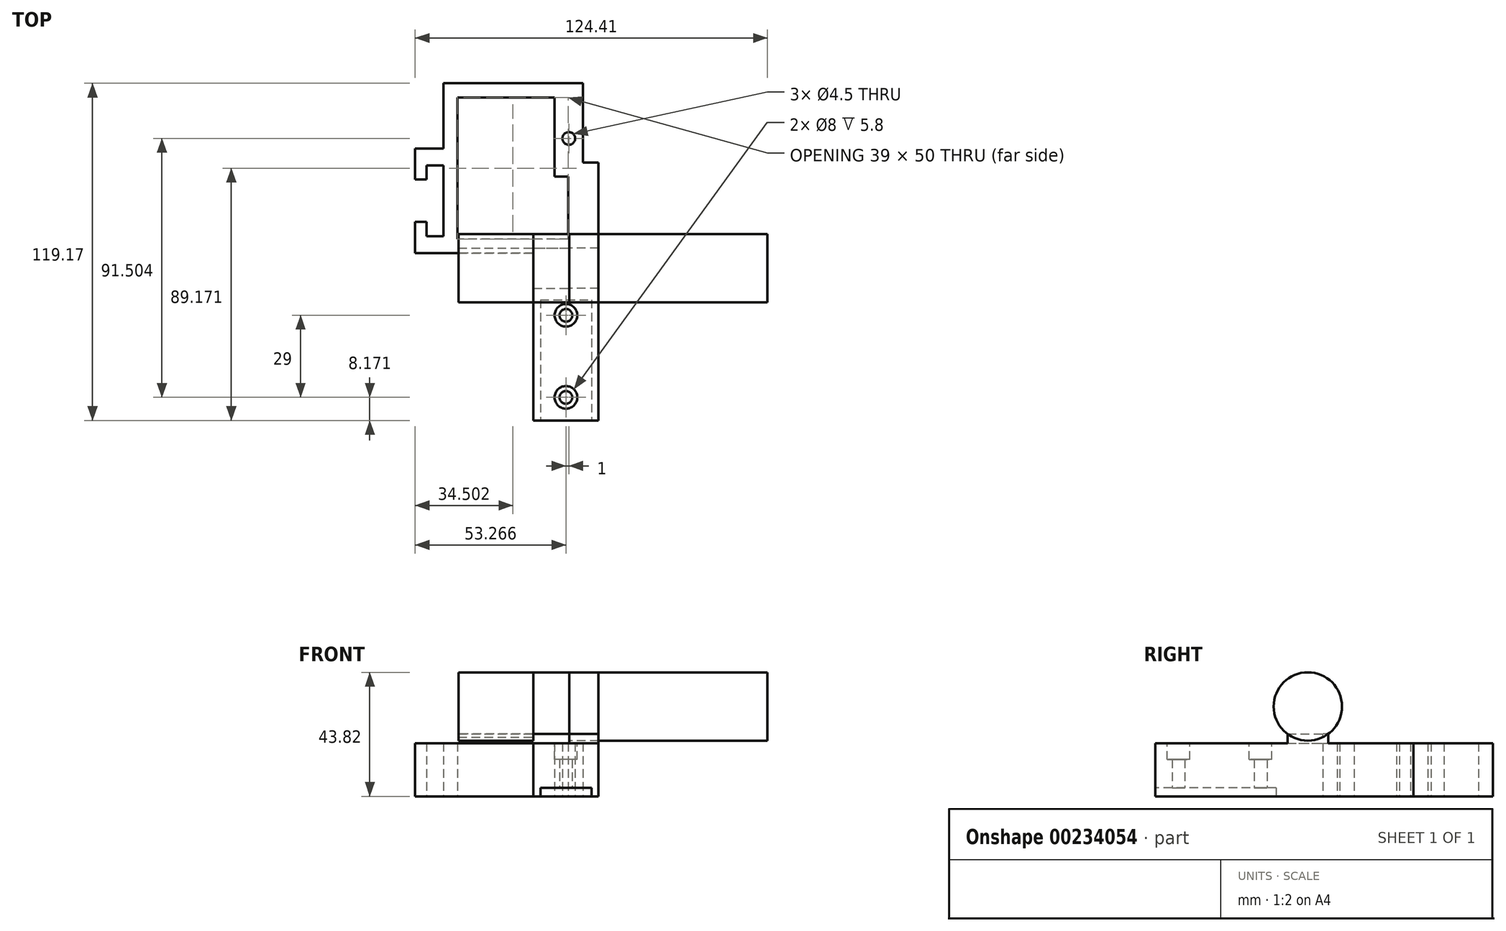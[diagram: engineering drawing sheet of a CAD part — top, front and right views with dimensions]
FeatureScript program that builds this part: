
annotation { "Feature Type Name" : "Feature", "Feature Type Description" : "" }
export const myFeature = defineFeature(function(context is Context, id is Id, definition is map)
    precondition{}
    {
        {
            var Q0;
            Q0=qCreatedBy(makeId("Top.planeOp"),FACE);
            var sketch = newSketch(context, id + "F0", { "sketchPlane" : qUnion([Q0])});
            skLineSegment(sketch, "E0.bottom", {"start": v(-42.14, 42.67) * mm, "end": v(-24.14, 42.67) * mm});
            skLineSegment(sketch, "E0.top", {"start": v(-42.14, 2.67) * mm, "end": v(-24.14, 2.67) * mm});
            skLineSegment(sketch, "E0.left", {"start": v(-42.14, 42.67) * mm, "end": v(-42.14, 2.67) * mm});
            skLineSegment(sketch, "E0.right", {"start": v(-24.14, 42.67) * mm, "end": v(-24.14, 2.67) * mm});
            skLineSegment(sketch, "E1", {"start": v(-33.14, 2.67) * mm, "end": v(-33.14, 77.67) * mm, "construction": true});
            skLineSegment(sketch, "E2", {"start": v(-33.14, 2.67) * mm, "end": v(-33.14, 90.67) * mm, "construction": true});
            skLineSegment(sketch, "E3", {"start": v(-33.14, 2.67) * mm, "end": v(-33.14, 99.67) * mm, "construction": true});
            skCircle(sketch, "E4", {"center": v(-32.14, 99.67) * mm, "radius": 2.25 * mm});
            skCircle(sketch, "E5", {"center": v(-33.14, 8.17) * mm, "radius": 2.25 * mm});
            skCircle(sketch, "E6", {"center": v(-33.14, 37.17) * mm, "radius": 2.25 * mm});
            skLineSegment(sketch, "E7", {"start": v(-32.14, 99.67) * mm, "end": v(-33.14, 99.67) * mm});
            skLineSegment(sketch, "E8", {"start": v(-33.14, 69.67) * mm, "end": v(-73.64, 69.67) * mm});
            skLineSegment(sketch, "E9", {"start": v(-73.64, 69.67) * mm, "end": v(-73.64, 77.67) * mm});
            skLineSegment(sketch, "E10", {"start": v(-73.64, 77.67) * mm, "end": v(-33.14, 77.67) * mm});
            skLineSegment(sketch, "E11", {"start": v(-33.14, 90.67) * mm, "end": v(-73.64, 90.67) * mm});
            skLineSegment(sketch, "E12", {"start": v(-73.64, 90.67) * mm, "end": v(-73.64, 82.67) * mm});
            skLineSegment(sketch, "E13", {"start": v(-73.64, 82.67) * mm, "end": v(-33.14, 82.67) * mm});
            skSolve(sketch);
        }
        {
            var Q0;
            Q0=qCreatedBy(makeId("Right.planeOp"),FACE);
            cPlane(context, id + "F1", {"entities" : qUnion([Q0]), "cplaneType" : CPlaneType.OFFSET, "offset" : 32 * mm, "oppositeDirection" : true, "width" : 150 * mm, "height" : 150 * mm});
        }
        {
            var Q0;
            Q0=qCreatedBy(makeId("Top.planeOp"),FACE);
            var sketch = newSketch(context, id + "F2", { "sketchPlane" : qUnion([Q0])});
            skLineSegment(sketch, "E14", {"start": v(-21.64, 0) * mm, "end": v(-44.64, 0) * mm});
            skLineSegment(sketch, "E15", {"start": v(-44.64, 0) * mm, "end": v(-44.64, 64.17) * mm});
            skLineSegment(sketch, "E16", {"start": v(-44.64, 64.17) * mm, "end": v(-71.4, 64.17) * mm});
            skLineSegment(sketch, "E17", {"start": v(-71.4, 64.17) * mm, "end": v(-71.4, 114.17) * mm});
            skLineSegment(sketch, "E18", {"start": v(-71.4, 114.17) * mm, "end": v(-21.64, 114.17) * mm});
            skLineSegment(sketch, "E19", {"start": v(-21.64, 114.17) * mm, "end": v(-21.64, 0) * mm});
            skLineSegment(sketch, "E20", {"start": v(-44.64, 64.17) * mm, "end": v(-32.4, 64.17) * mm});
            skLineSegment(sketch, "E21", {"start": v(-32.4, 64.17) * mm, "end": v(-32.4, 86.17) * mm});
            skLineSegment(sketch, "E22", {"start": v(-32.4, 86.17) * mm, "end": v(-37.1, 86.17) * mm});
            skLineSegment(sketch, "E23", {"start": v(-37.1, 86.17) * mm, "end": v(-37.1, 114.17) * mm});
            skLineSegment(sketch, "E24", {"start": v(-44.64, 59.17) * mm, "end": v(-76.4, 59.17) * mm});
            skLineSegment(sketch, "E25", {"start": v(-76.4, 59.17) * mm, "end": v(-76.4, 119.17) * mm});
            skLineSegment(sketch, "E26", {"start": v(-76.4, 119.17) * mm, "end": v(-21.64, 119.17) * mm});
            skLineSegment(sketch, "E27", {"start": v(-21.64, 114.17) * mm, "end": v(-21.64, 119.17) * mm});
            skLineSegment(sketch, "E28", {"start": v(-44.64, 59.17) * mm, "end": v(-21.64, 59.17) * mm});
            skLineSegment(sketch, "E29", {"start": v(-76.4, 59.17) * mm, "end": v(-86.4, 59.17) * mm});
            skLineSegment(sketch, "E30", {"start": v(-86.4, 59.17) * mm, "end": v(-86.4, 70.17) * mm});
            skLineSegment(sketch, "E31", {"start": v(-86.4, 70.17) * mm, "end": v(-82.4, 70.17) * mm});
            skLineSegment(sketch, "E32", {"start": v(-82.4, 70.17) * mm, "end": v(-82.4, 65.17) * mm});
            skLineSegment(sketch, "E33", {"start": v(-82.4, 65.17) * mm, "end": v(-76.4, 65.17) * mm});
            skLineSegment(sketch, "E34", {"start": v(-76.4, 90.17) * mm, "end": v(-82.4, 90.17) * mm});
            skLineSegment(sketch, "E35", {"start": v(-82.4, 90.17) * mm, "end": v(-82.4, 85.17) * mm});
            skLineSegment(sketch, "E36", {"start": v(-82.4, 85.17) * mm, "end": v(-86.4, 85.17) * mm});
            skLineSegment(sketch, "E37", {"start": v(-86.4, 85.17) * mm, "end": v(-86.4, 96.17) * mm});
            skLineSegment(sketch, "E38", {"start": v(-86.4, 96.17) * mm, "end": v(-76.4, 96.17) * mm});
            skLineSegment(sketch, "E39", {"start": v(-21.64, 91.17) * mm, "end": v(-27.18, 91.17) * mm});
            skLineSegment(sketch, "E40", {"start": v(-27.18, 91.17) * mm, "end": v(-27.18, 119.17) * mm});
            skSolve(sketch);
        }
        {
            var Q0;
            {var subQ7=sQuery(id+"F2.wireOp",EDGE,"E14");Q0=makeQuery(id+"F2.imprint","IMPRINT",FACE,{"disambiguationData":[TD([[makeQuery(id+"F2.imprint","IMPRINT",EDGE,{"derivedFrom":subQ7}),-1.0]])]});}
            var Q1;
            {var subQ6=sQuery(id+"F2.wireOp",EDGE,"E16");Q1=makeQuery(id+"F2.imprint","IMPRINT",FACE,{"disambiguationData":[TD([[makeQuery(id+"F2.imprint","IMPRINT",EDGE,{"derivedFrom":subQ6}),1.0]])]});}
            var Q2;
            {var subQ0=sQuery(id+"F2.wireOp",EDGE,"E20");Q2=makeQuery(id+"F2.imprint","IMPRINT",FACE,{"disambiguationData":[TD([[makeQuery(id+"F2.imprint","IMPRINT",EDGE,{"derivedFrom":subQ0}),-1.0]])]});}
            var Q3;
            {var subQ0=sQuery(id+"F2.wireOp",EDGE,"E34");Q3=makeQuery(id+"F2.imprint","IMPRINT",FACE,{"disambiguationData":[TD([[makeQuery(id+"F2.imprint","IMPRINT",EDGE,{"derivedFrom":subQ0}),-1.0]])]});}
            var Q4;
            {var subQ0=sQuery(id+"F2.wireOp",EDGE,"E29");Q4=makeQuery(id+"F2.imprint","IMPRINT",FACE,{"disambiguationData":[TD([[makeQuery(id+"F2.imprint","IMPRINT",EDGE,{"derivedFrom":subQ0}),-1.0]])]});}
            extrude(context, id + "F3", {"entities" : qUnion([Q0, Q1, Q2, Q3, Q4]), "depth" : 22 * mm, "offsetDistance" : 25 * mm});
        }
        {
            var Q0;
            Q0=qCreatedBy(id+"F1.planeOp",FACE);
            var sketch = newSketch(context, id + "F4", { "sketchPlane" : qUnion([Q0])});
            skCircle(sketch, "E41", {"center": v(53.85, 31.74) * mm, "radius": 12.08 * mm});
            skLineSegment(sketch, "E42", {"start": v(53.85, 31.74) * mm, "end": v(53.85, 0.3) * mm, "construction": true});
            skLineSegment(sketch, "E43", {"start": v(41.28, 22) * mm, "end": v(62.3, 22) * mm});
            skSolve(sketch);
        }
        {
            var Q0;
            {var subQ0=sQuery(id+"F4.wireOp",EDGE,"e8Y6q84t-d5iK-QpJX-XlCZ-QnJJpwHAz1ef");var subQ1=sQuery(id+"F4.wireOp",EDGE,"E41");var subQ2=makeQuery(id+"F4.imprint","INTERSECT",VERTEX,{"disambiguationData":[OD(0.0)],"derivedFrom":[subQ1,subQ0]});Q0=makeQuery(id+"F4.imprint","IMPRINT",FACE,{"disambiguationData":[TD([[makeQuery(id+"F4.imprint","IMPRINT",EDGE,{"disambiguationData":[TD([[subQ2,-1.0]])],"derivedFrom":subQ1}),1.0]])]});}
            var Q1;
            {var subQ0=sQuery(id+"F4.wireOp",EDGE,"077d775b-663c-4919-bb39-97218beeb0e60.MirrorCS");var subQ1=sQuery(id+"F4.wireOp",EDGE,"E41");var subQ2=makeQuery(id+"F4.imprint","INTERSECT",VERTEX,{"disambiguationData":[OD(0.0)],"derivedFrom":[subQ1,subQ0]});Q1=makeQuery(id+"F4.imprint","IMPRINT",FACE,{"disambiguationData":[TD([[makeQuery(id+"F4.imprint","IMPRINT",EDGE,{"disambiguationData":[TD([[subQ2,1.0]])],"derivedFrom":subQ1}),1.0]])]});}
            var Q2;
            {var subQ0=sQuery(id+"F4.wireOp",EDGE,"e8Y6q84t-d5iK-QpJX-XlCZ-QnJJpwHAz1ef");var subQ1=sQuery(id+"F4.wireOp",EDGE,"E41");var subQ2=makeQuery(id+"F4.imprint","INTERSECT",VERTEX,{"disambiguationData":[OD(1.0)],"derivedFrom":[subQ1,subQ0]});Q2=makeQuery(id+"F4.imprint","IMPRINT",FACE,{"disambiguationData":[TD([[makeQuery(id+"F4.imprint","IMPRINT",EDGE,{"disambiguationData":[TD([[subQ2,-1.0]])],"derivedFrom":subQ1}),1.0]])]});}
            var Q3;
            {var subQ0=sQuery(id+"F4.wireOp",EDGE,"E43");var subQ1=sQuery(id+"F4.wireOp",EDGE,"E41");var subQ2=makeQuery(id+"F4.imprint","INTERSECT",VERTEX,{"disambiguationData":[OD(0.0)],"derivedFrom":[subQ1,subQ0]});Q3=makeQuery(id+"F4.imprint","IMPRINT",FACE,{"disambiguationData":[TD([[makeQuery(id+"F4.imprint","IMPRINT",EDGE,{"disambiguationData":[TD([[subQ2,-1.0]])],"derivedFrom":subQ1}),1.0]])]});}
            extrude(context, id + "F5", {"entities" : qUnion([Q0, Q1, Q2, Q3]), "depth" : 70 * mm, "offsetDistance" : 25 * mm});
        }
        {
            var Q0;
            {var subQ5=sQuery(id+"F4.wireOp",EDGE,"E43");Q0=makeQuery(id+"F4.imprint","IMPRINT",FACE,{"disambiguationData":[TD([[makeQuery(id+"F4.imprint","IMPRINT",EDGE,{"derivedFrom":subQ5}),1.0]])]});}
            var Q1;
            Q1=makeQuery(id+"F3.opExtrude","SWEPT_FACE",FACE,{"disambiguationData":[OSD([sQuery(id+"F2.wireOp",EDGE,"E15")])]});
            extrude(context, id + "F6", {"entities" : qUnion([Q0]), "endBound" : BoundingType.UP_TO_SURFACE, "oppositeDirection" : true, "depth" : 20.4 * mm, "endBoundEntityFace" : qUnion([Q1]), "offsetDistance" : 25 * mm});
        }
        {
            var Q0;
            {var subQ5=sQuery(id+"F4.wireOp",EDGE,"E43");Q0=makeQuery(id+"F4.imprint","IMPRINT",FACE,{"disambiguationData":[TD([[makeQuery(id+"F4.imprint","IMPRINT",EDGE,{"derivedFrom":subQ5}),1.0]])]});}
            var Q1;
            Q1=makeQuery(id+"F3.opExtrude","SWEPT_FACE",FACE,{"disambiguationData":[OSD([sQuery(id+"F2.wireOp",EDGE,"E19")])]});
            extrude(context, id + "F7", {"entities" : qUnion([Q0]), "endBound" : BoundingType.UP_TO_SURFACE, "depth" : 25 * mm, "endBoundEntityFace" : qUnion([Q1]), "offsetDistance" : 25 * mm});
        }
        {
            var Q0;
            Q0=makeQuery(id+"F0.imprint","IMPRINT",FACE,{"disambiguationData":[TD([[makeQuery(id+"F0.imprint","IMPRINT",EDGE,{"derivedFrom":sQuery(id+"F0.wireOp",EDGE,"E0.bottom")}),-1.0]])]});
            extrude(context, id + "F8", {"entities" : qUnion([Q0]), "operationType" : NewBodyOperationType.REMOVE, "depth" : 3 * mm, "offsetDistance" : 25 * mm});
        }
        {
            var Q0;
            Q0=makeQuery(id+"F0.imprint","IMPRINT",FACE,{"disambiguationData":[TD([[makeQuery(id+"F0.imprint","IMPRINT",EDGE,{"derivedFrom":sQuery(id+"F0.wireOp",EDGE,"E5")}),1.0]])]});
            var Q1;
            Q1=makeQuery(id+"F0.imprint","IMPRINT",FACE,{"disambiguationData":[TD([[makeQuery(id+"F0.imprint","IMPRINT",EDGE,{"derivedFrom":sQuery(id+"F0.wireOp",EDGE,"E6")}),1.0]])]});
            var Q2;
            Q2=makeQuery(id+"F3.opExtrude","CAP_FACE",FACE,{"disambiguationData":[OSD([sQuery(id+"F2.wireOp",EDGE,"E14"),sQuery(id+"F2.wireOp",EDGE,"E15"),sQuery(id+"F2.wireOp",EDGE,"E16"),sQuery(id+"F2.wireOp",EDGE,"E17"),sQuery(id+"F2.wireOp",EDGE,"E18"),sQuery(id+"F2.wireOp",EDGE,"E19"),sQuery(id+"F2.wireOp",EDGE,"E20"),sQuery(id+"F2.wireOp",EDGE,"E21"),sQuery(id+"F2.wireOp",EDGE,"E22"),sQuery(id+"F2.wireOp",EDGE,"E23"),sQuery(id+"F2.wireOp",EDGE,"E24"),sQuery(id+"F2.wireOp",EDGE,"E25"),sQuery(id+"F2.wireOp",EDGE,"E26"),sQuery(id+"F2.wireOp",EDGE,"PEMW9tW5-gVqX-yNYE-Lq4t-Qgq4adK5CDRl"),sQuery(id+"F2.wireOp",EDGE,"D0Wptgma-Dwai-aCjx-Nw00-f0un8KthKtqb")])],"isStart":false});
            extrude(context, id + "F9", {"entities" : qUnion([Q0, Q1]), "operationType" : NewBodyOperationType.REMOVE, "endBound" : BoundingType.UP_TO_SURFACE, "depth" : 25 * mm, "endBoundEntityFace" : qUnion([Q2]), "offsetDistance" : 25 * mm});
        }
        {
            var Q0;
            Q0=makeQuery(id+"F0.imprint","IMPRINT",FACE,{"disambiguationData":[TD([[makeQuery(id+"F0.imprint","IMPRINT",EDGE,{"derivedFrom":sQuery(id+"F0.wireOp",EDGE,"E4")}),1.0]])]});
            extrude(context, id + "F10", {"entities" : qUnion([Q0]), "operationType" : NewBodyOperationType.REMOVE, "depth" : 19 * mm, "offsetDistance" : 25 * mm});
        }
        {
            var Q0;
            Q0=makeQuery(id+"F8.boolean.opBoolean","COPY",FACE,{"derivedFrom":makeQuery(id+"F8.opExtrude","SWEPT_FACE",FACE,{"disambiguationData":[OSD([sQuery(id+"F0.wireOp",EDGE,"E0.top")])]})});
            var Q1;
            Q1=makeQuery(id+"F3.opExtrude","SWEPT_FACE",FACE,{"disambiguationData":[OSD([sQuery(id+"F2.wireOp",EDGE,"E14")])]});
            extrude(context, id + "F11", {"entities" : qUnion([Q0]), "operationType" : NewBodyOperationType.REMOVE, "endBound" : BoundingType.UP_TO_SURFACE, "oppositeDirection" : true, "depth" : 25 * mm, "endBoundEntityFace" : qUnion([Q1]), "offsetDistance" : 25 * mm});
        }
        {
            var Q0;
            Q0=makeQuery(id+"F7.opExtrude","SWEPT_BODY",BODY,{"disambiguationData":[OSD([sQuery(id+"F4.wireOp",EDGE,"E41"),sQuery(id+"F4.wireOp",EDGE,"e8Y6q84t-d5iK-QpJX-XlCZ-QnJJpwHAz1ef"),sQuery(id+"F4.wireOp",EDGE,"077d775b-663c-4919-bb39-97218beeb0e60.MirrorCS"),sQuery(id+"F4.wireOp",EDGE,"E43")])]});
            var Q1;
            Q1=makeQuery(id+"F3.opExtrude","SWEPT_BODY",BODY,{"disambiguationData":[OSD([sQuery(id+"F2.wireOp",EDGE,"E14"),sQuery(id+"F2.wireOp",EDGE,"E15"),sQuery(id+"F2.wireOp",EDGE,"E16"),sQuery(id+"F2.wireOp",EDGE,"E17"),sQuery(id+"F2.wireOp",EDGE,"E18"),sQuery(id+"F2.wireOp",EDGE,"E19"),sQuery(id+"F2.wireOp",EDGE,"E20"),sQuery(id+"F2.wireOp",EDGE,"E21"),sQuery(id+"F2.wireOp",EDGE,"E22"),sQuery(id+"F2.wireOp",EDGE,"E23"),sQuery(id+"F2.wireOp",EDGE,"E24"),sQuery(id+"F2.wireOp",EDGE,"E25"),sQuery(id+"F2.wireOp",EDGE,"E26"),sQuery(id+"F2.wireOp",EDGE,"PEMW9tW5-gVqX-yNYE-Lq4t-Qgq4adK5CDRl"),sQuery(id+"F2.wireOp",EDGE,"D0Wptgma-Dwai-aCjx-Nw00-f0un8KthKtqb")])]});
            booleanBodies(context, id + "F12", {"operationType" : BooleanOperationType.UNION, "tools" : qUnion([Q0, Q1])});
        }
        {
            var Q0;
            {var subQ0=sQuery(id+"F2.wireOp",EDGE,"E19");var subQ1=sQuery(id+"F2.wireOp",EDGE,"E15");var subQ2=sQuery(id+"F2.wireOp",EDGE,"E14");Q0=makeQuery(id+"F12.opBoolean","SPLIT",FACE,{"disambiguationData":[TD([makeQuery(id+"F3.opExtrude","SWEPT_FACE",FACE,{"disambiguationData":[OSD([subQ2])]})])],"derivedFrom":makeQuery(id+"F3.opExtrude","CAP_FACE",FACE,{"disambiguationData":[OSD([subQ2,subQ1,sQuery(id+"F2.wireOp",EDGE,"E16"),sQuery(id+"F2.wireOp",EDGE,"E17"),sQuery(id+"F2.wireOp",EDGE,"E18"),subQ0,sQuery(id+"F2.wireOp",EDGE,"E20"),sQuery(id+"F2.wireOp",EDGE,"E21"),sQuery(id+"F2.wireOp",EDGE,"E22"),sQuery(id+"F2.wireOp",EDGE,"E23"),sQuery(id+"F2.wireOp",EDGE,"E24"),sQuery(id+"F2.wireOp",EDGE,"E25"),sQuery(id+"F2.wireOp",EDGE,"E26"),sQuery(id+"F2.wireOp",EDGE,"PEMW9tW5-gVqX-yNYE-Lq4t-Qgq4adK5CDRl"),sQuery(id+"F2.wireOp",EDGE,"D0Wptgma-Dwai-aCjx-Nw00-f0un8KthKtqb")])],"isStart":false})});}
            var sketch = newSketch(context, id + "F13", { "sketchPlane" : qUnion([Q0])});
            skCircle(sketch, "E44", {"center": v(-33.14, 37.17) * mm, "radius": 4 * mm});
            skCircle(sketch, "E45", {"center": v(-33.14, 8.17) * mm, "radius": 4 * mm});
            skSolve(sketch);
        }
        {
            var Q0;
            Q0 = qSketchRegion(id + "F13", true);
            extrude(context, id + "F14", {"entities" : qUnion([Q0]), "operationType" : NewBodyOperationType.REMOVE, "oppositeDirection" : true, "depth" : 9 * mm, "offsetDistance" : 25 * mm});
        }
        {
            var Q0;
            {var subQ0=sQuery(id+"F4.wireOp",EDGE,"e8Y6q84t-d5iK-QpJX-XlCZ-QnJJpwHAz1ef");var subQ1=sQuery(id+"F4.wireOp",EDGE,"E41");var subQ2=makeQuery(id+"F4.imprint","INTERSECT",VERTEX,{"disambiguationData":[OD(1.0)],"derivedFrom":[subQ1,subQ0]});Q0=makeQuery(id+"F4.imprint","IMPRINT",FACE,{"disambiguationData":[TD([[makeQuery(id+"F4.imprint","IMPRINT",EDGE,{"disambiguationData":[TD([[subQ2,-1.0]])],"derivedFrom":subQ1}),1.0]])]});}
            var Q1;
            {var subQ0=sQuery(id+"F4.wireOp",EDGE,"e8Y6q84t-d5iK-QpJX-XlCZ-QnJJpwHAz1ef");var subQ1=sQuery(id+"F4.wireOp",EDGE,"E41");var subQ2=makeQuery(id+"F4.imprint","INTERSECT",VERTEX,{"disambiguationData":[OD(0.0)],"derivedFrom":[subQ1,subQ0]});Q1=makeQuery(id+"F4.imprint","IMPRINT",FACE,{"disambiguationData":[TD([[makeQuery(id+"F4.imprint","IMPRINT",EDGE,{"disambiguationData":[TD([[subQ2,-1.0]])],"derivedFrom":subQ1}),1.0]])]});}
            var Q2;
            {var subQ0=sQuery(id+"F4.wireOp",EDGE,"077d775b-663c-4919-bb39-97218beeb0e60.MirrorCS");var subQ1=sQuery(id+"F4.wireOp",EDGE,"E41");var subQ2=makeQuery(id+"F4.imprint","INTERSECT",VERTEX,{"disambiguationData":[OD(0.0)],"derivedFrom":[subQ1,subQ0]});Q2=makeQuery(id+"F4.imprint","IMPRINT",FACE,{"disambiguationData":[TD([[makeQuery(id+"F4.imprint","IMPRINT",EDGE,{"disambiguationData":[TD([[subQ2,1.0]])],"derivedFrom":subQ1}),1.0]])]});}
            var Q3;
            {var subQ0=sQuery(id+"F4.wireOp",EDGE,"E43");var subQ1=sQuery(id+"F4.wireOp",EDGE,"E41");var subQ2=makeQuery(id+"F4.imprint","INTERSECT",VERTEX,{"disambiguationData":[OD(0.0)],"derivedFrom":[subQ1,subQ0]});Q3=makeQuery(id+"F4.imprint","IMPRINT",FACE,{"disambiguationData":[TD([[makeQuery(id+"F4.imprint","IMPRINT",EDGE,{"disambiguationData":[TD([[subQ2,-1.0]])],"derivedFrom":subQ1}),1.0]])]});}
            extrude(context, id + "F15", {"entities" : qUnion([Q0, Q1, Q2, Q3]), "oppositeDirection" : true, "depth" : 39.1 * mm, "offsetDistance" : 25 * mm});
        }
        {
            var Q0;
            {var subQ0=sQuery(id+"F2.wireOp",EDGE,"E38");var subQ1=sQuery(id+"F2.wireOp",EDGE,"E37");var subQ2=sQuery(id+"F2.wireOp",EDGE,"E36");var subQ3=sQuery(id+"F2.wireOp",EDGE,"E35");var subQ4=sQuery(id+"F2.wireOp",EDGE,"E34");var subQ6=sQuery(id+"F2.wireOp",EDGE,"E29");var subQ7=sQuery(id+"F2.wireOp",EDGE,"E24");var subQ8=sQuery(id+"F2.wireOp",EDGE,"E33");var subQ9=sQuery(id+"F2.wireOp",EDGE,"E32");var subQ10=sQuery(id+"F2.wireOp",EDGE,"E31");var subQ11=sQuery(id+"F2.wireOp",EDGE,"E30");var subQ12=sQuery(id+"F2.wireOp",EDGE,"E15");var subQ13=sQuery(id+"F2.wireOp",EDGE,"E26");var subQ14=sQuery(id+"F2.wireOp",EDGE,"E25");var subQ15=sQuery(id+"F2.wireOp",EDGE,"E18");var subQ16=sQuery(id+"F2.wireOp",EDGE,"E17");var subQ17=sQuery(id+"F2.wireOp",EDGE,"E20");var subQ18=sQuery(id+"F2.wireOp",EDGE,"E16");var subQ19=sQuery(id+"F2.wireOp",EDGE,"E27");var subQ20=sQuery(id+"F2.wireOp",EDGE,"E19");var subQ21=sQuery(id+"F2.wireOp",EDGE,"E21");var subQ22=sQuery(id+"F2.wireOp",EDGE,"E22");var subQ23=sQuery(id+"F2.wireOp",EDGE,"E23");Q0=makeQuery(id+"F12.opBoolean","SPLIT",FACE,{"disambiguationData":[TD([makeQuery(id+"F3.opExtrude","SWEPT_FACE",FACE,{"disambiguationData":[OSD([subQ16])]})])],"derivedFrom":makeQuery(id+"F3.opExtrude","CAP_FACE",FACE,{"disambiguationData":[OSD([sQuery(id+"F2.wireOp",EDGE,"E14"),subQ12,subQ18,subQ16,subQ15,subQ20,subQ17,subQ21,subQ22,subQ23,subQ7,subQ14,subQ13,subQ19,subQ6,subQ11,subQ10,subQ9,subQ8,subQ4,subQ3,subQ2,subQ1,subQ0])],"isStart":false})});}
            extrude(context, id + "F16", {"entities" : qUnion([Q0]), "operationType" : NewBodyOperationType.REMOVE, "oppositeDirection" : true, "depth" : 3.2 * mm, "offsetDistance" : 25 * mm});
        }
    });
